# Revit family: CHEMOWENT Ramka + Kratka Otwór Prostokątny
name_source: partatom
category: Duct Accessories
revit_build: Autodesk Revit 2015 (Build: 20140606_1530(x64)
units: mm (PartAtom-declared; Revit-internal decimal feet)

## types (32) — shared parameters
Default Elevation = 1219 mm
Manufacturer = CHEMOWENT
Materiał = CHEMOWENT - PVC-U

## per-type parameters (varying)
| type | B | H | Typ kratki | Typ ramki montażowej |
| 300×100 LG-A | 310 mm  [stored 1.01706 ft] | 110 mm  [stored 0.360892 ft] | CHEMOWENT Kratka LG-A : 300×100 | CHEMOWENT Ramka Montażowa : 300×100 |
| 300×150 LG-A | 310 mm  [stored 1.01706 ft] | 160 mm | CHEMOWENT Kratka LG-A : 300×150 | CHEMOWENT Ramka Montażowa : 300×150 |
| 300×200 LG-A | 310 mm  [stored 1.01706 ft] | 210 mm | CHEMOWENT Kratka LG-A : 300×200 | CHEMOWENT Ramka Montażowa : 300×200 |
| 300×250 LG-A | 310 mm  [stored 1.01706 ft] | 260 mm | CHEMOWENT Kratka LG-A : 300×250 | CHEMOWENT Ramka Montażowa : 300×250 |
| 400×100 LG-A | 410 mm | 110 mm  [stored 0.360892 ft] | CHEMOWENT Kratka LG-A : 400×100 | CHEMOWENT Ramka Montażowa : 400×100 |
| 400×150 LG-A | 410 mm | 160 mm | CHEMOWENT Kratka LG-A : 400×150 | CHEMOWENT Ramka Montażowa : 400×150 |
| 400×200 LG-A | 410 mm | 210 mm | CHEMOWENT Kratka LG-A : 400×200 | CHEMOWENT Ramka Montażowa : 400×200 |
| 400×250 LG-A | 410 mm | 260 mm | CHEMOWENT Kratka LG-A : 400×250 | CHEMOWENT Ramka Montażowa : 400×250 |
| 500×100 LG-A | 510 mm | 110 mm  [stored 0.360892 ft] | CHEMOWENT Kratka LG-A : 500×100 | CHEMOWENT Ramka Montażowa : 500×100 |
| 500×150 LG-A | 510 mm | 160 mm | CHEMOWENT Kratka LG-A : 500×150 | CHEMOWENT Ramka Montażowa : 500×150 |
| 500×200 LG-A | 510 mm | 210 mm | CHEMOWENT Kratka LG-A : 500×200 | CHEMOWENT Ramka Montażowa : 500×200 |
| 500×250 LG-A | 510 mm | 260 mm | CHEMOWENT Kratka LG-A : 500×250 | CHEMOWENT Ramka Montażowa : 500×250 |
| 600×100 LG-A | 610 mm | 110 mm  [stored 0.360892 ft] | CHEMOWENT Kratka LG-A : 600×100 | CHEMOWENT Ramka Montażowa : 600×100 |
| 600×150 LG-A | 610 mm | 160 mm | CHEMOWENT Kratka LG-A : 600×150 | CHEMOWENT Ramka Montażowa : 600×150 |
| 600×200 LG-A | 610 mm | 210 mm | CHEMOWENT Kratka LG-A : 600×200 | CHEMOWENT Ramka Montażowa : 600×200 |
| 600×250 LG-A | 610 mm | 260 mm | CHEMOWENT Kratka LG-A : 600×250 | CHEMOWENT Ramka Montażowa : 600×250 |
| 300×100 LG-C | 310 mm  [stored 1.01706 ft] | 110 mm  [stored 0.360892 ft] | CHEMOWENT Kratka LG-C : 300×100 | CHEMOWENT Ramka Montażowa : 300×100 |
| 300×150 LG-C | 310 mm  [stored 1.01706 ft] | 160 mm | CHEMOWENT Kratka LG-C : 300×150 | CHEMOWENT Ramka Montażowa : 300×150 |
| 300×200 LG-C | 310 mm  [stored 1.01706 ft] | 210 mm | CHEMOWENT Kratka LG-C : 300×200 | CHEMOWENT Ramka Montażowa : 300×200 |
| 300×250 LG-C | 310 mm  [stored 1.01706 ft] | 260 mm | CHEMOWENT Kratka LG-C : 300×250 | CHEMOWENT Ramka Montażowa : 300×250 |
| 400×100 LG-C | 410 mm | 110 mm  [stored 0.360892 ft] | CHEMOWENT Kratka LG-C : 400×100 | CHEMOWENT Ramka Montażowa : 400×100 |
| 400×150 LG-C | 410 mm | 160 mm | CHEMOWENT Kratka LG-C : 400×150 | CHEMOWENT Ramka Montażowa : 400×150 |
| 400×200 LG-C | 410 mm | 210 mm | CHEMOWENT Kratka LG-C : 400×200 | CHEMOWENT Ramka Montażowa : 400×200 |
| 400×250 LG-C | 410 mm | 260 mm | CHEMOWENT Kratka LG-C : 400×250 | CHEMOWENT Ramka Montażowa : 400×250 |
| 500×100 LG-C | 510 mm | 110 mm  [stored 0.360892 ft] | CHEMOWENT Kratka LG-C : 500×100 | CHEMOWENT Ramka Montażowa : 500×100 |
| 500×150 LG-C | 510 mm | 160 mm | CHEMOWENT Kratka LG-C : 500×150 | CHEMOWENT Ramka Montażowa : 500×150 |
| 500×200 LG-C | 510 mm | 210 mm | CHEMOWENT Kratka LG-C : 500×200 | CHEMOWENT Ramka Montażowa : 500×200 |
| 500×250 LG-C | 510 mm | 260 mm | CHEMOWENT Kratka LG-C : 500×250 | CHEMOWENT Ramka Montażowa : 500×250 |
| 600×100 LG-C | 610 mm | 110 mm  [stored 0.360892 ft] | CHEMOWENT Kratka LG-C : 600×100 | CHEMOWENT Ramka Montażowa : 600×100 |
| 600×150 LG-C | 610 mm | 160 mm | CHEMOWENT Kratka LG-C : 600×150 | CHEMOWENT Ramka Montażowa : 600×150 |
| 600×200 LG-C | 610 mm | 210 mm | CHEMOWENT Kratka LG-C : 600×200 | CHEMOWENT Ramka Montażowa : 600×200 |
| 600×250 LG-C | 610 mm | 260 mm | CHEMOWENT Kratka LG-C : 600×250 | CHEMOWENT Ramka Montażowa : 600×250 |

note: [stored X ft] marks values corroborated as IEEE doubles in the binary element streams (Revit-internal decimal feet)

## geometry (parser evidence)
native form markers: Blend x8
no freeform markers — native parametric forms only
